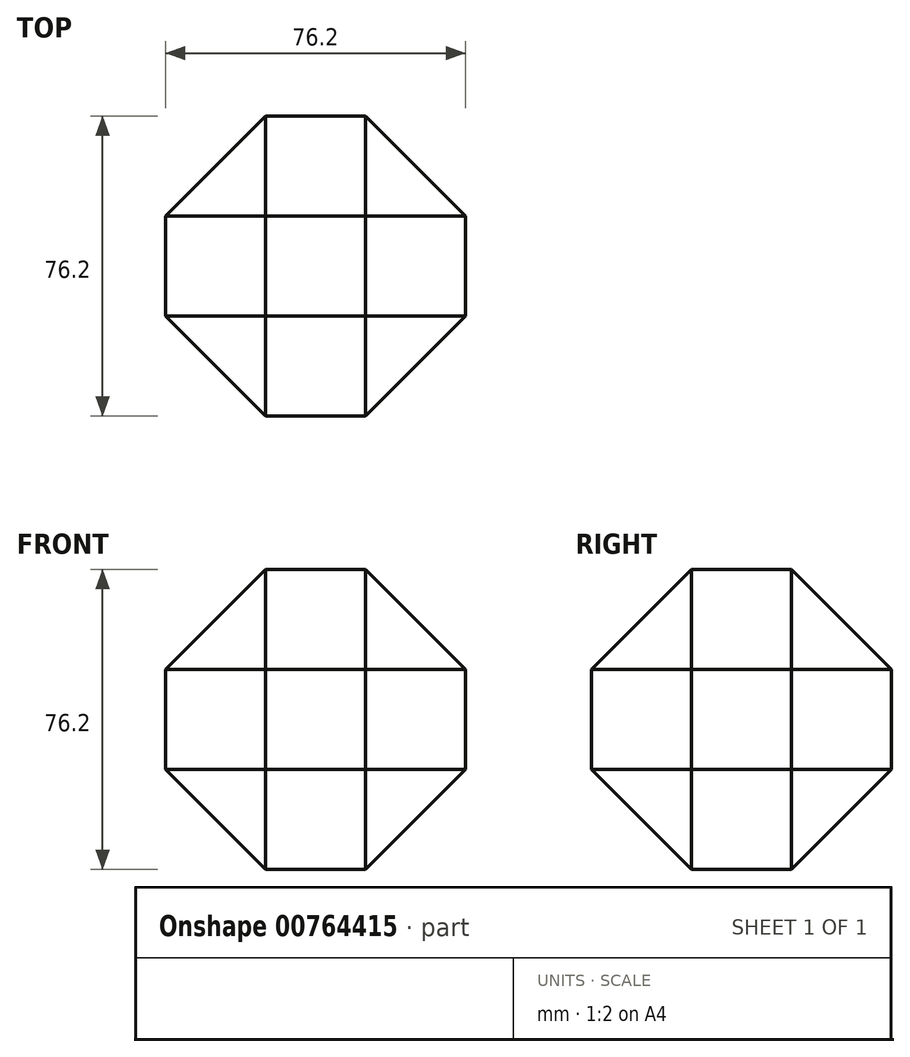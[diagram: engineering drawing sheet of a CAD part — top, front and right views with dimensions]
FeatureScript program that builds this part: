
annotation { "Feature Type Name" : "Feature", "Feature Type Description" : "" }
export const myFeature = defineFeature(function(context is Context, id is Id, definition is map)
    precondition{}
    {
        {
            var Q0;
            Q0=qCreatedBy(makeId("Top.planeOp"),FACE);
            var sketch = newSketch(context, id + "F0", { "sketchPlane" : qUnion([Q0])});
            skLineSegment(sketch, "E0.bottom", {"start": v(0, 0) * mm, "end": v(76.2, 0) * mm});
            skLineSegment(sketch, "E0.top", {"start": v(0, -76.2) * mm, "end": v(76.2, -76.2) * mm});
            skLineSegment(sketch, "E0.left", {"start": v(0, 0) * mm, "end": v(0, -76.2) * mm});
            skLineSegment(sketch, "E0.right", {"start": v(76.2, 0) * mm, "end": v(76.2, -76.2) * mm});
            skLineSegment(sketch, "E1", {"start": v(0, 0) * mm, "end": v(76.2, -76.2) * mm});
            skLineSegment(sketch, "E2", {"start": v(76.2, 0) * mm, "end": v(0, -76.2) * mm});
            skSolve(sketch);
        }
        {
            var Q0;
            Q0 = qSketchRegion(id + "F0", true);
            extrude(context, id + "F1", {"entities" : qUnion([Q0]), "depth" : 76.2 * mm, "offsetDistance" : 25.4 * mm});
        }
        {
            var Q0;
            Q0=makeQuery(id+"F1.opExtrude","CAP_EDGE",EDGE,{"disambiguationData":[OSD([sQuery(id+"F0.wireOp",EDGE,"E0.top")])],"isStart":false});
            var Q1;
            Q1=makeQuery(id+"F1.opExtrude","CAP_EDGE",EDGE,{"disambiguationData":[OSD([sQuery(id+"F0.wireOp",EDGE,"E0.bottom")])],"isStart":false});
            var Q2;
            Q2=makeQuery(id+"F1.opExtrude","SWEPT_FACE",FACE,{"disambiguationData":[OSD([sQuery(id+"F0.wireOp",EDGE,"E0.right")])]});
            var Q3;
            Q3=makeQuery(id+"F1.opExtrude","SWEPT_FACE",FACE,{"disambiguationData":[OSD([sQuery(id+"F0.wireOp",EDGE,"E0.top")])]});
            var Q4;
            Q4=makeQuery(id+"F1.opExtrude","CAP_FACE",FACE,{"disambiguationData":[OSD([sQuery(id+"F0.wireOp",EDGE,"E0.bottom"),sQuery(id+"F0.wireOp",EDGE,"E0.top"),sQuery(id+"F0.wireOp",EDGE,"E0.left"),sQuery(id+"F0.wireOp",EDGE,"E0.right")])],"isStart":true});
            var Q5;
            Q5=makeQuery(id+"F1.opExtrude","SWEPT_FACE",FACE,{"disambiguationData":[OSD([sQuery(id+"F0.wireOp",EDGE,"E0.left")])]});
            var Q6;
            Q6=makeQuery(id+"F1.opExtrude","CAP_FACE",FACE,{"disambiguationData":[OSD([sQuery(id+"F0.wireOp",EDGE,"E0.bottom"),sQuery(id+"F0.wireOp",EDGE,"E0.top"),sQuery(id+"F0.wireOp",EDGE,"E0.left"),sQuery(id+"F0.wireOp",EDGE,"E0.right")])],"isStart":false});
            chamfer(context, id + "F2", {"entities" : qUnion([Q0, Q1, Q2, Q3, Q4, Q5, Q6]), "width" : 25.4 * mm, "tangentPropagation" : true});
        }
    });
